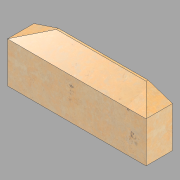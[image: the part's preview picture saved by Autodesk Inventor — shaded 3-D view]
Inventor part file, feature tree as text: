
AUTODESK INVENTOR PART (.ipt)
format: ipt  version: 2022.2 (Build 262287010, 287A)  size: 149,504 bytes
history: native  units: in
note: dims shown in document units (in); Inventor stores cm internally (conversion verified against a paired STEP export)
features: extrude x4, sketch x3
ambient origin geometry x8: Origin, YZ Plane, XZ Plane, XY Plane, X Axis, Y Axis, Z Axis, Center Point
bodies: Solid1 (feature_tree)
feature tree (7):
  extrude  "Extrusion1"  Depth=6.5in
  extrude  "Extrusion2"  Depth=12.0in
  sketch  "Sketch3"  dims[d5=2.0in d6=0.0in d7=0.0in d8=6.0in d9=2.0in d10=0.0in d11=0.0in d12=0.0in d13=0.0in]
  extrude  "Extrusion3"  TaperAngle=0.0deg  [1 undecoded]
  extrude  "Extrusion4"  Depth=6.0in
  sketch  "Sketch1"  dims[d0=34.0in d1=6.5in]
  sketch  "Sketch2"  dims[d2=12.0in d3=0.0in d4=0.5in]
note: 1 required parameter value undecoded (feature->parameter linkage not recoverable at this tier; creation-order binding heuristic only, values carry confidence <= 0.55)
